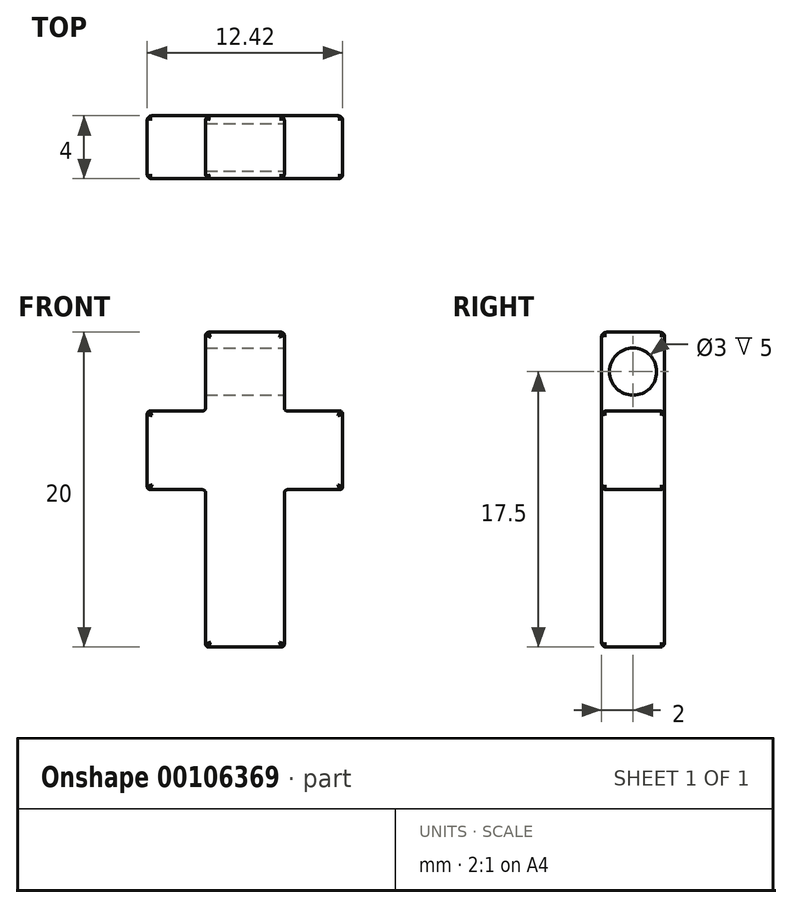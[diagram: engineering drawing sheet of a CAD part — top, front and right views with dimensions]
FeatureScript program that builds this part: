
annotation { "Feature Type Name" : "Feature", "Feature Type Description" : "" }
export const myFeature = defineFeature(function(context is Context, id is Id, definition is map)
    precondition{}
    {
        {
            var Q0;
            Q0=qCreatedBy(makeId("Front.planeOp"),FACE);
            var sketch = newSketch(context, id + "F0", { "sketchPlane" : qUnion([Q0])});
            skLineSegment(sketch, "E0", {"start": v(0, 0) * mm, "end": v(0, 100) * mm, "construction": true});
            skLineSegment(sketch, "E1.bottom", {"start": v(-62.1, 100) * mm, "end": v(62.1, 100) * mm, "construction": true});
            skLineSegment(sketch, "E1.top", {"start": v(-62.1, -100) * mm, "end": v(62.1, -100) * mm, "construction": true});
            skLineSegment(sketch, "E1.left", {"start": v(-62.1, 100) * mm, "end": v(-62.1, -100) * mm, "construction": true});
            skLineSegment(sketch, "E1.right", {"start": v(62.1, 100) * mm, "end": v(62.1, -100) * mm, "construction": true});
            skLineSegment(sketch, "E2", {"start": v(-62.1, 50) * mm, "end": v(62.1, 50) * mm, "construction": true});
            skLineSegment(sketch, "E3.0", {"start": v(25, 0) * mm, "end": v(25, 100) * mm, "construction": true});
            skLineSegment(sketch, "E4", {"start": v(0, 100) * mm, "end": v(23, 100) * mm});
            skLineSegment(sketch, "E5", {"start": v(27, 50) * mm, "end": v(60.1, 50) * mm});
            skLineSegment(sketch, "E6", {"start": v(60.1, 0) * mm, "end": v(27, 0) * mm});
            skLineSegment(sketch, "E7", {"start": v(25, 98) * mm, "end": v(25, 52) * mm});
            skLineSegment(sketch, "E8", {"start": v(62.1, 48) * mm, "end": v(62.1, 2) * mm});
            skLineSegment(sketch, "E9", {"start": v(25, -2) * mm, "end": v(25, -98) * mm});
            skLineSegment(sketch, "E10", {"start": v(23, -100) * mm, "end": v(0, -100) * mm});
            skPoint(sketch, "E11.visualSharp", {"position": v(25, 100) * mm});
            skArc(sketch, "E11.filletArc", {"start": v(25, 98) * mm, "mid": v(24.41, 99.41) * mm, "end": v(23, 100) * mm});
            skPoint(sketch, "E12.visualSharp", {"position": v(25, 50) * mm});
            skArc(sketch, "E12.filletArc", {"start": v(25, 52) * mm, "mid": v(25.59, 50.59) * mm, "end": v(27, 50) * mm});
            skPoint(sketch, "E13.visualSharp", {"position": v(62.1, 50) * mm});
            skArc(sketch, "E13.filletArc", {"start": v(62.1, 48) * mm, "mid": v(61.51, 49.41) * mm, "end": v(60.1, 50) * mm});
            skPoint(sketch, "E14.visualSharp", {"position": v(62.1, 0) * mm});
            skArc(sketch, "E14.filletArc", {"start": v(60.1, 0) * mm, "mid": v(61.51, 0.59) * mm, "end": v(62.1, 2) * mm});
            skPoint(sketch, "E15.visualSharp", {"position": v(25, 0) * mm});
            skArc(sketch, "E15.filletArc", {"start": v(27, 0) * mm, "mid": v(25.59, -0.59) * mm, "end": v(25, -2) * mm});
            skPoint(sketch, "E16.visualSharp", {"position": v(25, -100) * mm});
            skArc(sketch, "E16.filletArc", {"start": v(23, -100) * mm, "mid": v(24.41, -99.41) * mm, "end": v(25, -98) * mm});
            skLineSegment(sketch, "E17.MirrorCS", {"start": v(0, 100) * mm, "end": v(-23, 100) * mm});
            skLineSegment(sketch, "E18.MirrorCS", {"start": v(-25, 98) * mm, "end": v(-25, 52) * mm});
            skLineSegment(sketch, "E19.MirrorCS", {"start": v(-25, -2) * mm, "end": v(-25, -98) * mm});
            skArc(sketch, "E20.MirrorCS", {"start": v(-27, 0) * mm, "mid": v(-25.59, -0.59) * mm, "end": v(-25, -2) * mm});
            skLineSegment(sketch, "E21.MirrorCS", {"start": v(-60.1, 0) * mm, "end": v(-27, 0) * mm});
            skPoint(sketch, "E22.MirrorP", {"position": v(-62.1, 0) * mm});
            skArc(sketch, "E23.MirrorCS", {"start": v(-60.1, 0) * mm, "mid": v(-61.51, 0.59) * mm, "end": v(-62.1, 2) * mm});
            skLineSegment(sketch, "E24.MirrorCS", {"start": v(-62.1, 48) * mm, "end": v(-62.1, 2) * mm});
            skLineSegment(sketch, "E25.MirrorCS", {"start": v(-23, -100) * mm, "end": v(0, -100) * mm});
            skArc(sketch, "E26.MirrorCS", {"start": v(-23, -100) * mm, "mid": v(-24.41, -99.41) * mm, "end": v(-25, -98) * mm});
            skLineSegment(sketch, "E27.MirrorCS", {"start": v(-27, 50) * mm, "end": v(-60.1, 50) * mm});
            skArc(sketch, "E28.MirrorCS", {"start": v(-62.1, 48) * mm, "mid": v(-61.51, 49.41) * mm, "end": v(-60.1, 50) * mm});
            skArc(sketch, "E29.MirrorCS", {"start": v(-25, 52) * mm, "mid": v(-25.59, 50.59) * mm, "end": v(-27, 50) * mm});
            skArc(sketch, "E30.MirrorCS", {"start": v(-25, 98) * mm, "mid": v(-24.41, 99.41) * mm, "end": v(-23, 100) * mm});
            skSolve(sketch);
        }
        {
            var Q0;
            Q0=makeQuery(id+"F0.imprint","IMPRINT",FACE,{"disambiguationData":[TD([[makeQuery(id+"F0.imprint","IMPRINT",EDGE,{"derivedFrom":sQuery(id+"F0.wireOp",EDGE,"E4")}),-1.0]])]});
            extrude(context, id + "F1", {"entities" : qUnion([Q0]), "depth" : 40 * mm});
        }
        {
            var Q0;
            Q0=makeQuery(id+"F1.opExtrude","CAP_EDGE",EDGE,{"disambiguationData":[OSD([sQuery(id+"F0.wireOp",EDGE,"E7")])],"isStart":false});
            var Q1;
            Q1=makeQuery(id+"F1.opExtrude","CAP_EDGE",EDGE,{"disambiguationData":[OSD([sQuery(id+"F0.wireOp",EDGE,"E7")])],"isStart":true});
            fillet(context, id + "F2", {"entities" : qUnion([Q0, Q1]), "radius" : 3 * mm, "tangentPropagation" : true, "allowEdgeOverflow" : false});
        }
        {
            var Q0;
            Q0=makeQuery(id+"F1.opExtrude","SWEPT_BODY",BODY,{"disambiguationData":[OSD([sQuery(id+"F0.wireOp",EDGE,"E4"),sQuery(id+"F0.wireOp",EDGE,"E5"),sQuery(id+"F0.wireOp",EDGE,"E6"),sQuery(id+"F0.wireOp",EDGE,"E7"),sQuery(id+"F0.wireOp",EDGE,"E8"),sQuery(id+"F0.wireOp",EDGE,"E9"),sQuery(id+"F0.wireOp",EDGE,"E10"),sQuery(id+"F0.wireOp",EDGE,"E11.filletArc"),sQuery(id+"F0.wireOp",EDGE,"E12.filletArc"),sQuery(id+"F0.wireOp",EDGE,"E13.filletArc"),sQuery(id+"F0.wireOp",EDGE,"E14.filletArc"),sQuery(id+"F0.wireOp",EDGE,"E15.filletArc"),sQuery(id+"F0.wireOp",EDGE,"E16.filletArc"),sQuery(id+"F0.wireOp",EDGE,"E17.MirrorCS"),sQuery(id+"F0.wireOp",EDGE,"E18.MirrorCS"),sQuery(id+"F0.wireOp",EDGE,"E19.MirrorCS"),sQuery(id+"F0.wireOp",EDGE,"E20.MirrorCS"),sQuery(id+"F0.wireOp",EDGE,"E21.MirrorCS"),sQuery(id+"F0.wireOp",EDGE,"E23.MirrorCS"),sQuery(id+"F0.wireOp",EDGE,"E24.MirrorCS"),sQuery(id+"F0.wireOp",EDGE,"E25.MirrorCS"),sQuery(id+"F0.wireOp",EDGE,"E26.MirrorCS"),sQuery(id+"F0.wireOp",EDGE,"E27.MirrorCS"),sQuery(id+"F0.wireOp",EDGE,"E28.MirrorCS"),sQuery(id+"F0.wireOp",EDGE,"E29.MirrorCS"),sQuery(id+"F0.wireOp",EDGE,"E30.MirrorCS")])]});
            var Q1;
            Q1=qCreatedBy(makeId("Origin.pointOp"),VERTEX);
            transform(context, id + "F3", {"entities" : qUnion([Q0]), "transformType" : TransformType.SCALE_UNIFORMLY, "scale" : 1 / 10, "scalePoint" : qUnion([Q1]), "makeCopy" : false});
        }
        {
            var Q0;
            Q0=makeQuery(id+"F1.opExtrude","SWEPT_FACE",FACE,{"disambiguationData":[OSD([sQuery(id+"F0.wireOp",EDGE,"E7")])]});
            var sketch = newSketch(context, id + "F4", { "sketchPlane" : qUnion([Q0])});
            skLineSegment(sketch, "E31", {"start": v(-3.7, 9.8) * mm, "end": v(-0.3, 5.2) * mm, "construction": true});
            skCircle(sketch, "E32", {"center": v(-2, 7.5) * mm, "radius": 1.5 * mm});
            skSolve(sketch);
        }
        {
            var Q0;
            Q0=makeQuery(id+"F4.imprint","IMPRINT",FACE,{"disambiguationData":[TD([[makeQuery(id+"F4.imprint","IMPRINT",EDGE,{"derivedFrom":sQuery(id+"F4.wireOp",EDGE,"E32")}),1.0]])]});
            extrude(context, id + "F5", {"entities" : qUnion([Q0]), "operationType" : NewBodyOperationType.REMOVE, "endBound" : BoundingType.THROUGH_ALL, "oppositeDirection" : true, "depth" : 25 * mm});
        }
    });
